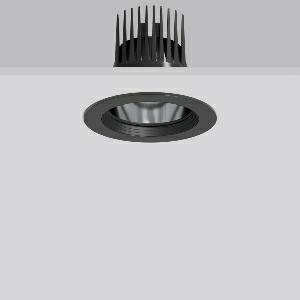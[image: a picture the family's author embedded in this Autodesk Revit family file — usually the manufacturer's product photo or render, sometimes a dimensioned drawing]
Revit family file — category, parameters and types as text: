
# Revit family: heledon_maxi_e_901763_003_3_b082
name_source: partatom
category: Lighting Fixtures
units: mm (PartAtom-declared; Revit-internal decimal feet)

## family parameters
Cut with Voids When Loaded = No
Host = Face
Light Source = No
Part Type = Normal
Room Calculation Point = No
Round Connector Dimension = Use Diameter
Shared = No

## types (1)
- HELEDON maxi E (1 x LED Modul 935, 4250 lm, 3500)
    Apparent Load = 35 VA
    Approval mark = CE
    CIE Flux Codes = 100 100 100 100 100
    Color Rendering = 92
    Color Temperature = 3500
    Default Elevation = 1800 mm
    Description = Series: HELEDON maxi
Round recessed downlight. Housing: die-cast aluminium, powder-coated. Black plastic ring and recessed LED to prevent glare from the side. Optical assembly with reflector made of MIRO-Silver with 98% total light reflection for outstanding efficiency - can be changed without tools. Best colour rendering index Ra>90. Suitable for Recessed ceiling mounting. Installation without tools thanks to spring fastening system. Including separate LED converter with connecting cable 600 mm.High quality converter without flickering and stroboscopic effect. Through-wiring box (5 pole) available as accessory. The following accessories can be mounted without use of tools: interchangeable lenses, decorative glasses, honeycomb louvre, clear and frosted diffusers, white interchangeable plastic ring. 
Colour: deep black, matt (RAL 9005)
Diameter: 162 mm
Height: 3 mm
Cut-out diameter: 152 mm
Recess height: 200 mm
Luminaire: recess height: 135 mm
Lamp: LED
Socket: without socket
Colour temperature: 3500K
Colour rendering index (CRI): 92
System power: 35 W
Rated luminous flux: 4250 lm
Luminous efficiency: 121 lm/W
Control gear: Regulated power supply
Protection class: II
Type of protection: IP 20
    Height = 0 mm  [stored 0 ft]
    Lamp = 1 x LED Modul 935
    Lamp Light Flux = 4250 lm
    Lamp count = 1
    Length = 162 mm
    Lifetime = 50000 h
    Luminous efficacy = 121 lm/W
    Manufacturer = RZB
    ModVariant = No
    Model = 901763.003.3
    Mounting Place = Ceiling
    Mounting Type = Recessed
    Number of Poles = 1
    OnlyDefault = Yes
    Power Factor = 1
    Product Name = HELEDON maxi E
    Product group = Recessed downlights
    ProductGroupID = 402
    Protection Class = Protection class II
    Protection Degree = IP 20
    RLX_Detail_Level = 1
    RLX_Emergency_Light_Flux = 0 lm
    RLX_Emergency_Type = 0
    RLX_Emergency_Type_DB = No
    RlxData = <blob elided: 123869 chars, md5=d7d472f8>
    Socket = socket
    Standby Power = 0 W
    System Light Flux = 4250 lm
    System Power = 35 W
    Type Comments = Product without accessories
    Type Image = 901662.003.jpg
    URL = http://relux.com
    VarID = ---
    Voltage = 230 V
    Voltage Range = 220-240 V
    Weight = 0.00 kg
    Width = 0 mm  [stored 0 ft]

note: [stored X ft] marks values corroborated as IEEE doubles in the binary element streams (Revit-internal decimal feet)

## geometry (parser evidence)
native form markers: Blend x4, Sweep x12
no freeform markers — native parametric forms only
